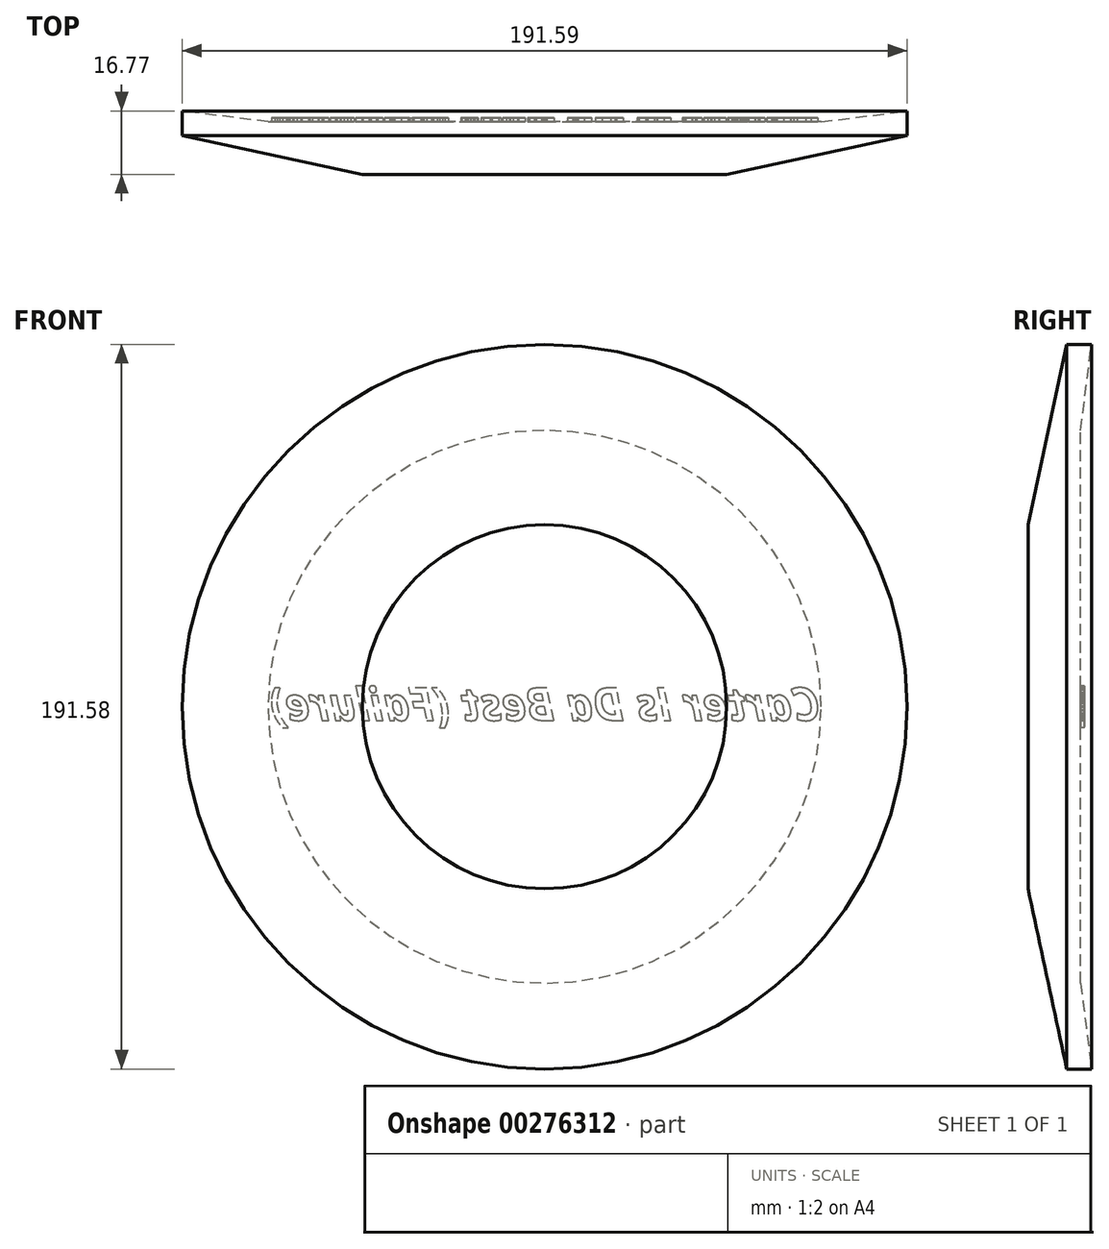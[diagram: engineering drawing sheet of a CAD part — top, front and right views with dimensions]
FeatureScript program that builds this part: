
annotation { "Feature Type Name" : "Feature", "Feature Type Description" : "" }
export const myFeature = defineFeature(function(context is Context, id is Id, definition is map)
    precondition{}
    {
        {
            var Q0;
            Q0=qCreatedBy(makeId("Top.planeOp"),FACE);
            var sketch = newSketch(context, id + "F0", { "sketchPlane" : qUnion([Q0])});
            skLineSegment(sketch, "E0.bottom", {"start": v(-7.06, -16.77) * mm, "end": v(41.08, -16.77) * mm});
            skLineSegment(sketch, "E1", {"start": v(41.08, -16.77) * mm, "end": v(41.08, -2.86) * mm});
            skLineSegment(sketch, "E2", {"start": v(41.08, -2.86) * mm, "end": v(-32.01, -2.86) * mm});
            skLineSegment(sketch, "E3", {"start": v(-32.01, -2.86) * mm, "end": v(-54.72, 0) * mm});
            skLineSegment(sketch, "E4", {"start": v(-54.72, 0) * mm, "end": v(-54.72, -6.56) * mm});
            skLineSegment(sketch, "E5", {"start": v(-54.72, -6.56) * mm, "end": v(-7.06, -16.77) * mm});
            skSolve(sketch);
        }
        {
            var Q0;
            Q0 = qSketchRegion(id + "F0", true);
            var Q1;
            Q1=sQuery(id+"F0.wireOp",EDGE,"E1");
            revolve(context, id + "F1", {"entities" : qUnion([Q0]), "axis" : qUnion([Q1]), "revolveType" : RevolveType.FULL});
        }
        {
            var Q0;
            Q0=makeQuery(id+"F1.opRevolve","SWEPT_FACE",FACE,{"disambiguationData":[OSD([sQuery(id+"F0.wireOp",EDGE,"E2")])]});
            var sketch = newSketch(context, id + "F2", { "sketchPlane" : qUnion([Q0])});
            skText(sketch, "E6", { "text": "Carter Is Da Best (Failure)", "fontName": "OpenSans-BoldItalic.ttf"});
            const initialGuessF2  = {"E6": [-0.11399, -0.00359, 1, 0, 0.00862]};
            skSetInitialGuess(sketch, initialGuessF2);
            skSolve(sketch);
        }
        {
            var Q0;
            Q0 = qSketchRegion(id + "F2", true);
            extrude(context, id + "F3", {"entities" : qUnion([Q0]), "operationType" : NewBodyOperationType.ADD, "depth" : 1 * mm});
        }
    });
